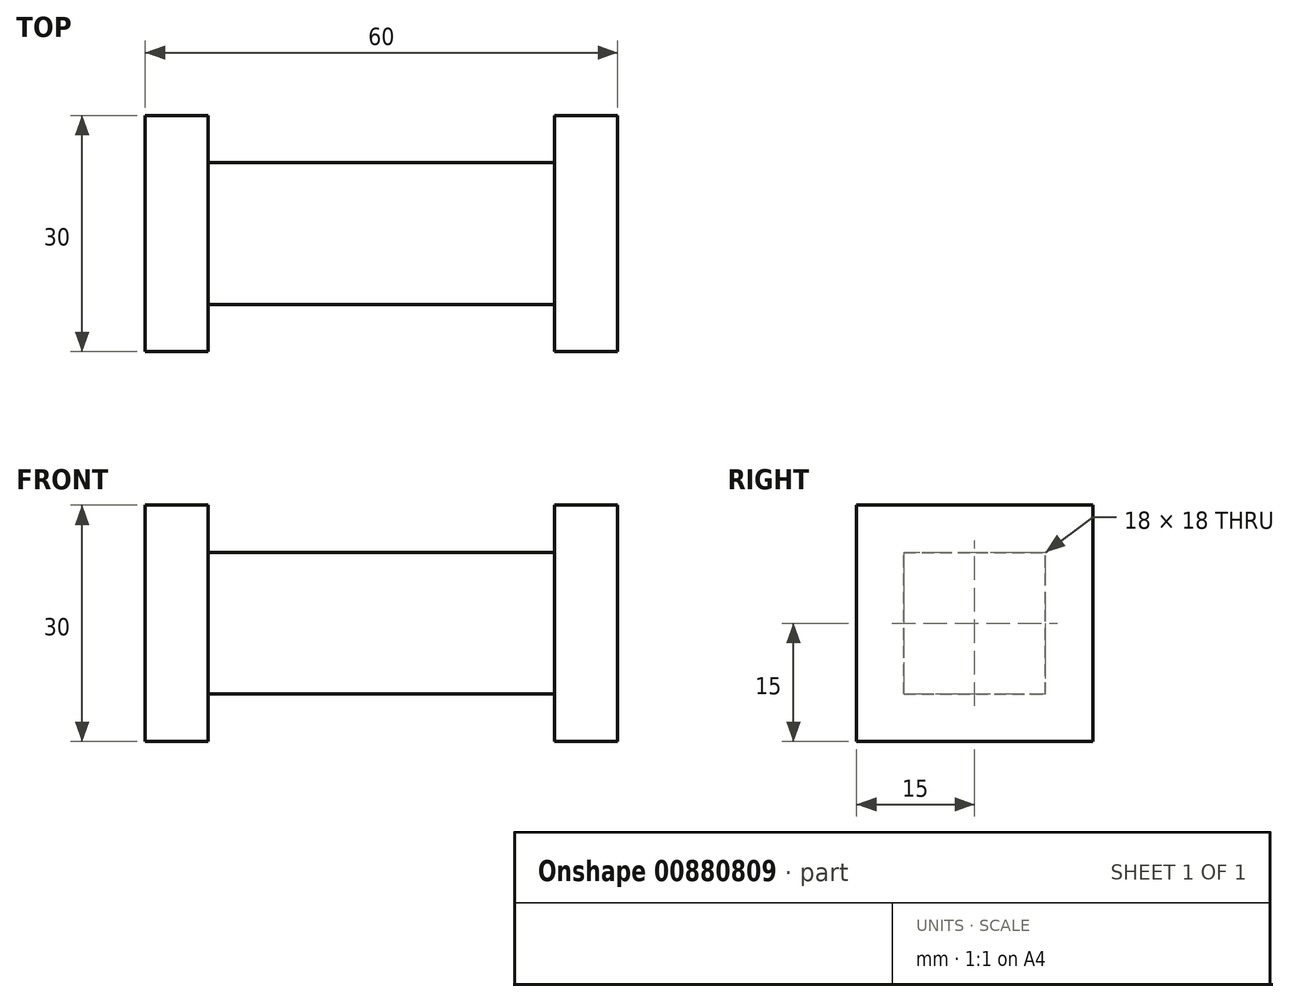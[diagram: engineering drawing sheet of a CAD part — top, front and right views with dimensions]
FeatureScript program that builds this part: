
annotation { "Feature Type Name" : "Feature", "Feature Type Description" : "" }
export const myFeature = defineFeature(function(context is Context, id is Id, definition is map)
    precondition{}
    {
        {
            var Q0;
            Q0=qCreatedBy(makeId("Front.planeOp"),FACE);
            var sketch = newSketch(context, id + "F0", { "sketchPlane" : qUnion([Q0])});
            skLineSegment(sketch, "E0.bottom", {"start": v(-30, 15) * mm, "end": v(30, 15) * mm});
            skLineSegment(sketch, "E0.top", {"start": v(-30, -15) * mm, "end": v(30, -15) * mm});
            skLineSegment(sketch, "E0.left", {"start": v(-30, 15) * mm, "end": v(-30, -15) * mm});
            skLineSegment(sketch, "E0.right", {"start": v(30, 15) * mm, "end": v(30, -15) * mm});
            skSolve(sketch);
        }
        {
            var Q0;
            Q0=makeQuery(id+"F0.imprint","IMPRINT",FACE,{"disambiguationData":[TD([[makeQuery(id+"F0.imprint","IMPRINT",EDGE,{"derivedFrom":sQuery(id+"F0.wireOp",EDGE,"E0.bottom")}),-1.0]])]});
            extrude(context, id + "F1", {"entities" : qUnion([Q0]), "depth" : 30 * mm, "offsetDistance" : 25 * mm});
        }
        {
            var Q0;
            Q0=makeQuery(id+"F1.opExtrude","CAP_FACE",FACE,{"disambiguationData":[OSD([sQuery(id+"F0.wireOp",EDGE,"E0.bottom"),sQuery(id+"F0.wireOp",EDGE,"E0.top"),sQuery(id+"F0.wireOp",EDGE,"E0.left"),sQuery(id+"F0.wireOp",EDGE,"E0.right")])],"isStart":false});
            var sketch = newSketch(context, id + "F2", { "sketchPlane" : qUnion([Q0])});
            skLineSegment(sketch, "E1.bottom", {"start": v(-22, -15) * mm, "end": v(22, -15) * mm});
            skLineSegment(sketch, "E1.top", {"start": v(-22, 15) * mm, "end": v(22, 15) * mm});
            skLineSegment(sketch, "E1.left", {"start": v(-22, -15) * mm, "end": v(-22, 15) * mm});
            skLineSegment(sketch, "E1.right", {"start": v(22, -15) * mm, "end": v(22, 15) * mm});
            skPoint(sketch, "E2.startSnap0", {"position": v(0, -12) * mm});
            skPoint(sketch, "E3.startSnap0", {"position": v(0, 7) * mm});
            skSolve(sketch);
        }
        {
            var Q0;
            Q0=makeQuery(id+"F2.imprint","IMPRINT",FACE,{"disambiguationData":[TD([[makeQuery(id+"F2.imprint","IMPRINT",EDGE,{"derivedFrom":sQuery(id+"F2.wireOp",EDGE,"E1.bottom")}),1.0]])]});
            extrude(context, id + "F3", {"entities" : qUnion([Q0]), "operationType" : NewBodyOperationType.REMOVE, "oppositeDirection" : true, "depth" : 6 * mm, "offsetDistance" : 25 * mm});
        }
        {
            var Q0;
            Q0=makeQuery(id+"F1.opExtrude","SWEPT_FACE",FACE,{"disambiguationData":[OSD([sQuery(id+"F0.wireOp",EDGE,"E0.top")])]});
            var sketch = newSketch(context, id + "F4", { "sketchPlane" : qUnion([Q0])});
            skLineSegment(sketch, "E4.bottom", {"start": v(22, 24) * mm, "end": v(-22, 24) * mm});
            skLineSegment(sketch, "E4.top", {"start": v(22, 0) * mm, "end": v(-22, 0) * mm});
            skLineSegment(sketch, "E4.left", {"start": v(22, 24) * mm, "end": v(22, 0) * mm});
            skLineSegment(sketch, "E4.right", {"start": v(-22, 24) * mm, "end": v(-22, 0) * mm});
            skSolve(sketch);
        }
        {
            var Q0;
            Q0=makeQuery(id+"F4.imprint","IMPRINT",FACE,{"disambiguationData":[TD([[makeQuery(id+"F4.imprint","IMPRINT",EDGE,{"derivedFrom":sQuery(id+"F4.wireOp",EDGE,"E4.bottom")}),-1.0]])]});
            extrude(context, id + "F5", {"entities" : qUnion([Q0]), "operationType" : NewBodyOperationType.REMOVE, "oppositeDirection" : true, "depth" : 6 * mm, "offsetDistance" : 25 * mm});
        }
        {
            var Q0;
            Q0=makeQuery(id+"F1.opExtrude","CAP_FACE",FACE,{"disambiguationData":[OSD([sQuery(id+"F0.wireOp",EDGE,"E0.bottom"),sQuery(id+"F0.wireOp",EDGE,"E0.top"),sQuery(id+"F0.wireOp",EDGE,"E0.left"),sQuery(id+"F0.wireOp",EDGE,"E0.right")])],"isStart":true});
            var sketch = newSketch(context, id + "F6", { "sketchPlane" : qUnion([Q0])});
            skLineSegment(sketch, "E5.bottom", {"start": v(-22, -9) * mm, "end": v(22, -9) * mm});
            skLineSegment(sketch, "E5.top", {"start": v(-22, 15) * mm, "end": v(22, 15) * mm});
            skLineSegment(sketch, "E5.left", {"start": v(-22, -9) * mm, "end": v(-22, 15) * mm});
            skLineSegment(sketch, "E5.right", {"start": v(22, -9) * mm, "end": v(22, 15) * mm});
            skSolve(sketch);
        }
        {
            var Q0;
            Q0=makeQuery(id+"F6.imprint","IMPRINT",FACE,{"disambiguationData":[TD([[makeQuery(id+"F6.imprint","IMPRINT",EDGE,{"derivedFrom":sQuery(id+"F6.wireOp",EDGE,"E5.bottom")}),-1.0]])]});
            extrude(context, id + "F7", {"entities" : qUnion([Q0]), "operationType" : NewBodyOperationType.REMOVE, "oppositeDirection" : true, "depth" : 6 * mm, "offsetDistance" : 25 * mm});
        }
        {
            var Q0;
            Q0=makeQuery(id+"F1.opExtrude","SWEPT_FACE",FACE,{"disambiguationData":[OSD([sQuery(id+"F0.wireOp",EDGE,"E0.bottom")])]});
            var sketch = newSketch(context, id + "F8", { "sketchPlane" : qUnion([Q0])});
            skLineSegment(sketch, "E6.bottom", {"start": v(-22, -24) * mm, "end": v(22, -24) * mm});
            skLineSegment(sketch, "E6.top", {"start": v(-22, -6) * mm, "end": v(22, -6) * mm});
            skLineSegment(sketch, "E6.left", {"start": v(-22, -24) * mm, "end": v(-22, -6) * mm});
            skLineSegment(sketch, "E6.right", {"start": v(22, -24) * mm, "end": v(22, -6) * mm});
            skSolve(sketch);
        }
        {
            var Q0;
            Q0=makeQuery(id+"F8.imprint","IMPRINT",FACE,{"disambiguationData":[TD([[makeQuery(id+"F8.imprint","IMPRINT",EDGE,{"derivedFrom":sQuery(id+"F8.wireOp",EDGE,"E6.bottom")}),1.0]])]});
            extrude(context, id + "F9", {"entities" : qUnion([Q0]), "operationType" : NewBodyOperationType.REMOVE, "oppositeDirection" : true, "depth" : 6 * mm, "offsetDistance" : 25 * mm});
        }
    });
